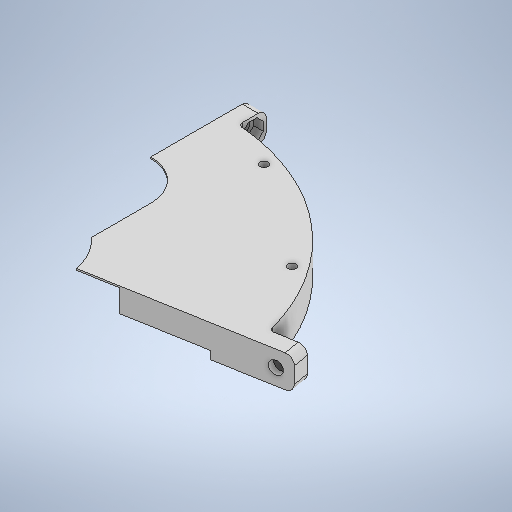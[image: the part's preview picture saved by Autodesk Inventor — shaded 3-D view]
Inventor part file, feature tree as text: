
AUTODESK INVENTOR PART (.ipt)
format: ipt  version: 2025 (Build 290162000, 162)  size: 416,768 bytes
history: native  units: in
note: dims shown in document units (in); Inventor stores cm internally (conversion verified against a paired STEP export)
features: sketch x15, extrude x11, hole x3, fillet x1
ambient origin geometry x8: Origin, YZ Plane, XZ Plane, XY Plane, X Axis, Y Axis, Z Axis, Center Point
bodies: Solid1 (feature_tree)
feature tree (30):
  extrude  "Extrusion1"  Depth=8.6614in
  extrude  "Extrusion2"  Depth=1.4173in
  extrude  "Extrusion3"  TaperAngle=0.0deg  [1 undecoded]
  extrude  "Extrusion4"  Depth=0.7874in
  hole  "Hole1"  [1 undecoded]
  extrude  "Extrusion5"  Depth=10.0394in
  extrude  "Extrusion6"  Depth=0.1575in TaperAngle=360.0deg
  extrude  "Extrusion7"  Depth=0.3937in TaperAngle=0.0deg
  extrude  "Extrusion8"  Depth=0.5512in TaperAngle=0.0deg
  extrude  "Extrusion9"  TaperAngle=0.0deg  [1 undecoded]
  extrude  "Extrusion10"  Depth=0.6693in
  hole  "Hole2"  [1 undecoded]
  extrude  "Extrusion11"  Depth=0.3937in
  hole  "Hole3"  [1 undecoded]
  fillet  "Fillet2"  Radius=0.2362in
  sketch  "Sketch1"  dims[d0=10.6299in d1=8.6614in]
  sketch  "Sketch2"  dims[d5=0.1969in d6=0.0in d7=0.0in]
  sketch  "Sketch3"  dims[d8=0.7874in d9=0.0in d10=2.7559in]
  sketch  "Sketch4"  dims[d11=0.7874in d12=7.874in]
  sketch  "Sketch5"  dims[d13=0.0in d14=0.0in d15=10.0394in]
  sketch  "Sketch Circular Pattern1"  dims[d2=2.1654in d3=0.0in d4=1.4173in]
  sketch  "Sketch6"  dims[d16=0.1575in d17=3.937in d19=360.0deg]
  sketch  "Sketch7"  dims[d21=0.1969in d22=0.3937in d23=0.4094in d24=0.0787in d25=90.0deg d26=0.315in d27=0.8108in d28=0.5906in d29=0.0in]
  sketch  "Sketch8"  dims[d30=2.9528in d33=0.0394in d34=0.0in d38=0.5512in d39=0.0in]
  sketch  "Sketch9"  dims[d40=0.5497in d41=0.0in d42=0.0in]
  sketch  "Sketch10"  dims[d43=0.7677in d44=0.6693in]
  sketch  "Sketch11"  dims[d45=0.6693in d46=0.1969in]
  sketch  "Sketch12"  dims[d47=0.3937in d48=0.0in d50=0.3346in]
  sketch  "Sketch13"  dims[d51=0.3346in d52=0.5197in d53=0.2362in d54=0.0in]
  sketch  "Sketch14"  dims[d55=0.3346in d56=0.3346in d57=0.3228in d58=0.2362in d59=0.5197in d60=0.2362in d61=90.0deg d62=0.315in d63=0.8108in d64=0.8858in d65=0.7874in d66=0.7874in d67=0.1969in d68=0.3937in d69=0.0in d70=0.3937in d71=0.3937in d72=0.3228in d73=0.2362in d74=0.5197in d75=0.2362in d76=90.0deg d77=0.315in d78=0.8108in d79=0.0984in]
note: 5 required parameter values undecoded (feature->parameter linkage not recoverable at this tier; creation-order binding heuristic only, values carry confidence <= 0.55)
